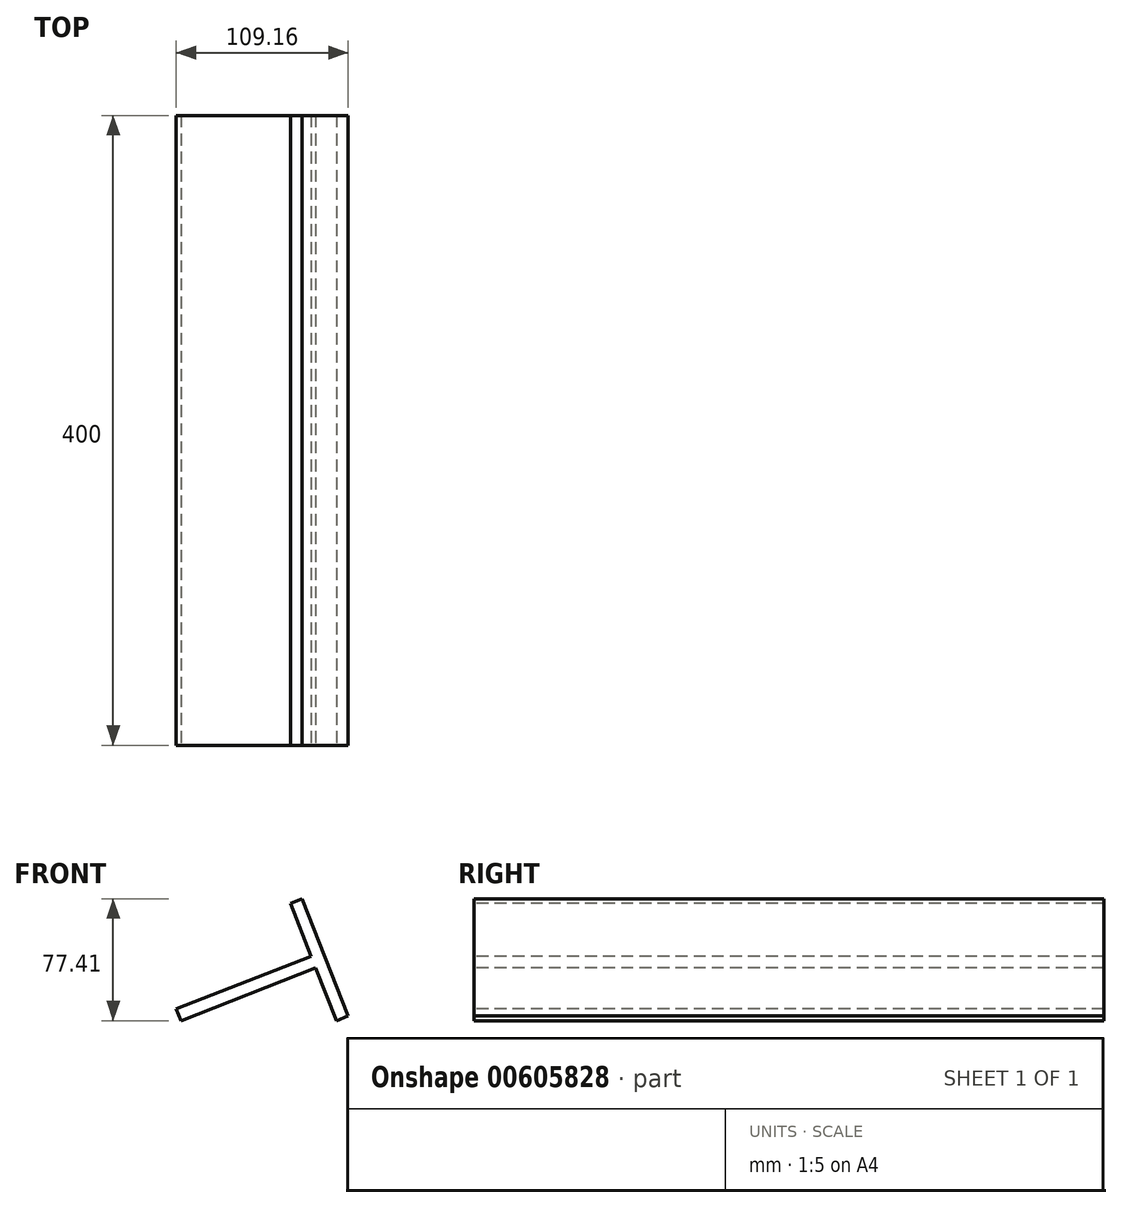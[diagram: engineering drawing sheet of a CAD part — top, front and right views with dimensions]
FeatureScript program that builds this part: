
annotation { "Feature Type Name" : "Feature", "Feature Type Description" : "" }
export const myFeature = defineFeature(function(context is Context, id is Id, definition is map)
    precondition{}
    {
        {
            var Q0;
            Q0=qCreatedBy(makeId("Front.planeOp"),FACE);
            var sketch = newSketch(context, id + "F0", { "sketchPlane" : qUnion([Q0])});
            skLineSegment(sketch, "E0", {"start": v(-77.1, 0) * mm, "end": v(8.58, 33.52) * mm});
            skLineSegment(sketch, "E1", {"start": v(8.58, 33.52) * mm, "end": v(21.7, 0) * mm});
            skLineSegment(sketch, "E2", {"start": v(21.7, 0) * mm, "end": v(29.15, 2.92) * mm});
            skLineSegment(sketch, "E3", {"start": v(5.67, 40.97) * mm, "end": v(-80, 7.45) * mm});
            skLineSegment(sketch, "E4", {"start": v(-80, 7.45) * mm, "end": v(-77.1, 0) * mm});
            skLineSegment(sketch, "E5", {"start": v(5.67, 40.97) * mm, "end": v(-7.45, 74.5) * mm});
            skLineSegment(sketch, "E6", {"start": v(-7.45, 74.5) * mm, "end": v(0, 77.41) * mm});
            skLineSegment(sketch, "E7", {"start": v(0, 77.41) * mm, "end": v(29.15, 2.92) * mm});
            skSolve(sketch);
        }
        {
            var Q0;
            Q0=qSketchRegion(id+"F0",true);
            extrude(context, id + "F1", {"entities" : qUnion([Q0]), "oppositeDirection" : true, "depth" : 400 * mm, "offsetDistance" : 25 * mm});
        }
        {
            var Q0;
            Q0=makeQuery(id+"F1.opExtrude","SWEPT_EDGE",EDGE,{"disambiguationData":[OSD([sQuery(id+"F0.wireOp",EDGE,"E2"),sQuery(id+"F0.wireOp",EDGE,"kCxIQD3j-peui-bjzT-GgCT-IUnZ7d8mdIaB")])]});
            cPoint(context, id + "F2", {"entities" : qUnion([Q0]), "parameter" : 0.5});
        }
        {
            var Q0;
            Q0=qCreatedBy(makeId("Front.planeOp"),FACE);
            var Q1;
            Q1=qCreatedBy(id+"F2",VERTEX);
            cPlane(context, id + "F3", {"entities" : qUnion([Q0, Q1]), "cplaneType" : CPlaneType.PLANE_POINT, "offset" : 25 * mm, "width" : 150 * mm, "height" : 150 * mm});
        }
        {
            var Q0;
            Q0=qCreatedBy(id+"F3.planeOp",FACE);
            var sketch = newSketch(context, id + "F4", { "sketchPlane" : qUnion([Q0])});
            skFitSpline(sketch, "E8", {"points": [v(15.64, 64.9) * mm, v(1.38, 83.6) * mm, v(-12.54, 79.25) * mm, v(-16.02, 43.23) * mm], "startDerivative": vector(-21.06, 50.15) * mm, "endDerivative": vector(-61.65, -28.44) * mm});
            skSolve(sketch);
        }
        {
            var Q0;
            Q0=sQuery(id+"F4.wireOp",VERTEX,"E8.0.internal");
            var Q1;
            Q1=makeQuery(id+"F1.opExtrude","SWEPT_FACE",FACE,{"disambiguationData":[OSD([sQuery(id+"F0.wireOp",EDGE,"E7")])]});
            cPlane(context, id + "F5", {"entities" : qUnion([Q0, Q1]), "cplaneType" : CPlaneType.PLANE_POINT, "offset" : 25 * mm, "width" : 150 * mm, "height" : 150 * mm});
        }
        {
            var Q0;
            Q0=qCreatedBy(id+"F5.planeOp",FACE);
            var sketch = newSketch(context, id + "F6", { "sketchPlane" : qUnion([Q0])});
            skLineSegment(sketch, "E9", {"start": v(200, 54.73) * mm, "end": v(200, 21.2) * mm});
            skLineSegment(sketch, "E10", {"start": v(203.5, 17.5) * mm, "end": v(221.44, 17.5) * mm});
            skFitSpline(sketch, "E11", {"points": [v(203.5, 17.5) * mm, v(201.38, 17.84) * mm, v(200.28, 18.95) * mm, v(200, 21.2) * mm], "startDerivative": vector(-10.25, 0.2) * mm, "endDerivative": vector(-0.2, 9) * mm});
            skSolve(sketch);
        }
        {
            var Q0;
            Q0=makeQuery(id+"F1.opExtrude","SWEPT_FACE",FACE,{"disambiguationData":[OSD([sQuery(id+"F0.wireOp",EDGE,"E3")])]});
            var Q1;
            Q1=sQuery(id+"F4.wireOp",VERTEX,"E8.end");
            cPlane(context, id + "F7", {"entities" : qUnion([Q0, Q1]), "cplaneType" : CPlaneType.PLANE_POINT, "offset" : 25 * mm, "width" : 150 * mm, "height" : 150 * mm});
        }
        {
            var Q0;
            Q0=qCreatedBy(id+"F7.planeOp",FACE);
            var sketch = newSketch(context, id + "F8", { "sketchPlane" : qUnion([Q0])});
            skLineSegment(sketch, "E12", {"start": v(0.84, 200) * mm, "end": v(-15.91, 200) * mm});
            skLineSegment(sketch, "E13", {"start": v(-18.63, 204.43) * mm, "end": v(-18.63, 222.34) * mm});
            skFitSpline(sketch, "E14", {"points": [v(-18.63, 204.43) * mm, v(-18.31, 201.48) * mm, v(-17.6, 200.6) * mm, v(-15.91, 200) * mm], "startDerivative": vector(-0.04, -12.45) * mm, "endDerivative": vector(6.01, -0.29) * mm});
            skSolve(sketch);
        }
        {
            var Q0;
            Q0=qCreatedBy(makeId("Front.planeOp"),FACE);
            var Q1;
            Q1=sQuery(id+"F6.wireOp",VERTEX,"E10.end");
            cPlane(context, id + "F9", {"entities" : qUnion([Q0, Q1]), "cplaneType" : CPlaneType.PLANE_POINT, "offset" : 25 * mm, "width" : 150 * mm, "height" : 150 * mm});
        }
        {
            var Q0;
            Q0=qCreatedBy(id+"F9.planeOp",FACE);
            var sketch = newSketch(context, id + "F10", { "sketchPlane" : qUnion([Q0])});
            skCircle(sketch, "E15", {"center": v(29.2, 30.22) * mm, "radius": 1.5 * mm});
            skSolve(sketch);
        }
        {
            var Q0;
            Q0=qSketchRegion(id+"F10",true);
            var Q1;
            Q1=qConstructionFilter(qBodyType(qCreatedBy(id+"F10",EDGE),BodyType.WIRE),ConstructionObject.NO);
            var Q2;
            Q2 = qConstructionFilter(qBodyType(qCreatedBy(id + "F6" ,EDGE), BodyType.WIRE), ConstructionObject.NO);
            var Q3;
            Q3 = qConstructionFilter(qBodyType(qCreatedBy(id + "F4" ,EDGE), BodyType.WIRE), ConstructionObject.NO);
            var Q4;
            Q4 = qConstructionFilter(qBodyType(qCreatedBy(id + "F8" ,EDGE), BodyType.WIRE), ConstructionObject.NO);
            sweep(context, id + "F11", {"bodyType" : ToolBodyType.SURFACE, "profiles" : qUnion([Q0]), "surfaceProfiles" : qUnion([Q1]), "path" : qUnion([Q2, Q3, Q4])});
        }
    });
